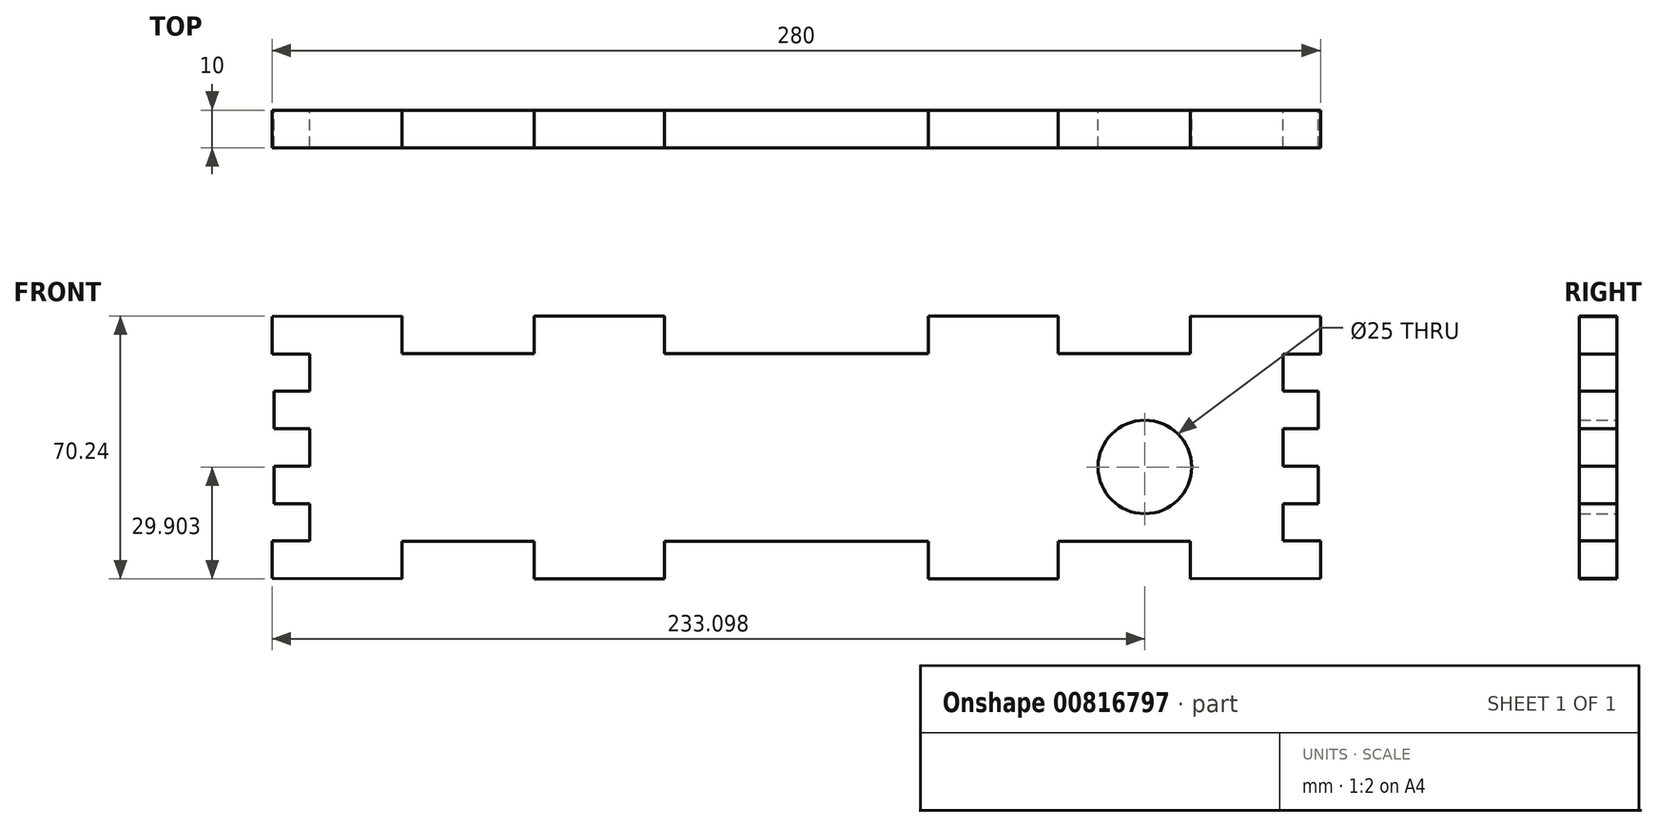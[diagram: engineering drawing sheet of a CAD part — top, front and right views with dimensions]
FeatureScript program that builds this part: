
annotation { "Feature Type Name" : "Feature", "Feature Type Description" : "" }
export const myFeature = defineFeature(function(context is Context, id is Id, definition is map)
    precondition{}
    {
        {
            var Q0;
            Q0=qCreatedBy(makeId("Front.planeOp"),FACE);
            var sketch = newSketch(context, id + "F0", { "sketchPlane" : qUnion([Q0])});
            skPoint(sketch, "E0.MirrorP", {"position": v(122.5, 95) * mm});
            skPoint(sketch, "E1.MirrorP", {"position": v(122.5, -95) * mm});
            skLineSegment(sketch, "E2", {"start": v(140, -35) * mm, "end": v(140, -25) * mm});
            skLineSegment(sketch, "E3", {"start": v(140, -25) * mm, "end": v(130, -25) * mm});
            skLineSegment(sketch, "E4", {"start": v(130, -25) * mm, "end": v(130, -15) * mm});
            skLineSegment(sketch, "E5", {"start": v(130, -15) * mm, "end": v(139.43, -15) * mm});
            skLineSegment(sketch, "E6", {"start": v(139.43, -15) * mm, "end": v(139.43, -5) * mm});
            skLineSegment(sketch, "E7", {"start": v(139.43, -5) * mm, "end": v(130, -5) * mm});
            skLineSegment(sketch, "E8.MirrorCS", {"start": v(139.43, 5) * mm, "end": v(130, 5) * mm});
            skLineSegment(sketch, "E9.MirrorCS", {"start": v(139.43, 15) * mm, "end": v(139.43, 5) * mm});
            skLineSegment(sketch, "E10.MirrorCS", {"start": v(130, 15) * mm, "end": v(139.43, 15) * mm});
            skLineSegment(sketch, "E11.MirrorCS", {"start": v(130, 25) * mm, "end": v(130, 15) * mm});
            skLineSegment(sketch, "E12.MirrorCS", {"start": v(140, 25) * mm, "end": v(130, 25) * mm});
            skLineSegment(sketch, "E13.MirrorCS", {"start": v(140, 35) * mm, "end": v(140, 25) * mm});
            skLineSegment(sketch, "E14.MirrorCS", {"start": v(-140, 35) * mm, "end": v(-140, 25) * mm});
            skLineSegment(sketch, "E15.MirrorCS", {"start": v(-140, -35) * mm, "end": v(-140, -25) * mm});
            skLineSegment(sketch, "E16.MirrorCS", {"start": v(-139.43, 15) * mm, "end": v(-139.43, 5) * mm});
            skLineSegment(sketch, "E17.MirrorCS", {"start": v(-139.43, -5) * mm, "end": v(-130, -5) * mm});
            skLineSegment(sketch, "E18.MirrorCS", {"start": v(-140, -25) * mm, "end": v(-130, -25) * mm});
            skLineSegment(sketch, "E19.MirrorCS", {"start": v(-130, -15) * mm, "end": v(-139.43, -15) * mm});
            skLineSegment(sketch, "E20.MirrorCS", {"start": v(-130, 15) * mm, "end": v(-139.43, 15) * mm});
            skLineSegment(sketch, "E21.MirrorCS", {"start": v(-140, 25) * mm, "end": v(-130, 25) * mm});
            skLineSegment(sketch, "E22.MirrorCS", {"start": v(-130, -25) * mm, "end": v(-130, -15) * mm});
            skLineSegment(sketch, "E23.MirrorCS", {"start": v(-139.43, -15) * mm, "end": v(-139.43, -5) * mm});
            skLineSegment(sketch, "E24.MirrorCS", {"start": v(-130, 25) * mm, "end": v(-130, 15) * mm});
            skLineSegment(sketch, "E25.MirrorCS", {"start": v(-139.43, 5) * mm, "end": v(-130, 5) * mm});
            skLineSegment(sketch, "E26", {"start": v(-130, 5) * mm, "end": v(-130, -5) * mm});
            skLineSegment(sketch, "E27", {"start": v(130, 5) * mm, "end": v(130, -5) * mm});
            skLineSegment(sketch, "E28", {"start": v(-140, -35) * mm, "end": v(-105.25, -35.12) * mm});
            skLineSegment(sketch, "E29", {"start": v(-105.25, -35.12) * mm, "end": v(-105.25, -25.12) * mm});
            skLineSegment(sketch, "E30", {"start": v(-105.25, -25.12) * mm, "end": v(-70, -25.12) * mm});
            skLineSegment(sketch, "E31", {"start": v(-70, -25.12) * mm, "end": v(-70, -35.12) * mm});
            skLineSegment(sketch, "E32", {"start": v(-70, -35.12) * mm, "end": v(-35.25, -35.12) * mm});
            skLineSegment(sketch, "E33", {"start": v(-35.25, -35.12) * mm, "end": v(-35.25, -25.12) * mm});
            skLineSegment(sketch, "E34", {"start": v(-35.25, -25.12) * mm, "end": v(0, -25.12) * mm});
            skLineSegment(sketch, "E35.MirrorCS", {"start": v(140, -35) * mm, "end": v(105.25, -35.12) * mm});
            skLineSegment(sketch, "E36.MirrorCS", {"start": v(105.25, -35.12) * mm, "end": v(105.25, -25.12) * mm});
            skLineSegment(sketch, "E37.MirrorCS", {"start": v(105.25, -25.12) * mm, "end": v(70, -25.12) * mm});
            skLineSegment(sketch, "E38.MirrorCS", {"start": v(70, -25.12) * mm, "end": v(70, -35.12) * mm});
            skLineSegment(sketch, "E39.MirrorCS", {"start": v(70, -35.12) * mm, "end": v(35.25, -35.12) * mm});
            skLineSegment(sketch, "E40.MirrorCS", {"start": v(35.25, -35.12) * mm, "end": v(35.25, -25.12) * mm});
            skLineSegment(sketch, "E41.MirrorCS", {"start": v(35.25, -25.12) * mm, "end": v(0, -25.12) * mm});
            skLineSegment(sketch, "E42.MirrorCS", {"start": v(-140, 35) * mm, "end": v(-105.25, 35.12) * mm});
            skLineSegment(sketch, "E43.MirrorCS", {"start": v(-105.25, 25.12) * mm, "end": v(-70, 25.12) * mm});
            skLineSegment(sketch, "E44.MirrorCS", {"start": v(-70, 25.12) * mm, "end": v(-70, 35.12) * mm});
            skLineSegment(sketch, "E45.MirrorCS", {"start": v(-105.25, 35.12) * mm, "end": v(-105.25, 25.12) * mm});
            skLineSegment(sketch, "E46.MirrorCS", {"start": v(-70, 35.12) * mm, "end": v(-35.25, 35.12) * mm});
            skLineSegment(sketch, "E47.MirrorCS", {"start": v(-35.25, 35.12) * mm, "end": v(-35.25, 25.12) * mm});
            skLineSegment(sketch, "E48.MirrorCS", {"start": v(-35.25, 25.12) * mm, "end": v(0, 25.12) * mm});
            skLineSegment(sketch, "E49.MirrorCS", {"start": v(35.25, 25.12) * mm, "end": v(0, 25.12) * mm});
            skLineSegment(sketch, "E50.MirrorCS", {"start": v(35.25, 35.12) * mm, "end": v(35.25, 25.12) * mm});
            skLineSegment(sketch, "E51.MirrorCS", {"start": v(70, 35.12) * mm, "end": v(35.25, 35.12) * mm});
            skLineSegment(sketch, "E52.MirrorCS", {"start": v(70, 25.12) * mm, "end": v(70, 35.12) * mm});
            skLineSegment(sketch, "E53.MirrorCS", {"start": v(105.25, 25.12) * mm, "end": v(70, 25.12) * mm});
            skLineSegment(sketch, "E54.MirrorCS", {"start": v(105.25, 35.12) * mm, "end": v(105.25, 25.12) * mm});
            skLineSegment(sketch, "E55.MirrorCS", {"start": v(140, 35) * mm, "end": v(105.25, 35.12) * mm});
            skCircle(sketch, "E56", {"center": v(93.1, -5.22) * mm, "radius": 12.5 * mm});
            skSolve(sketch);
        }
        {
            var Q0;
            Q0=makeQuery(id+"F0.imprint","IMPRINT",FACE,{"disambiguationData":[TD([[makeQuery(id+"F0.imprint","IMPRINT",EDGE,{"derivedFrom":sQuery(id+"F0.wireOp",EDGE,"E2")}),1.0]])]});
            extrude(context, id + "F1", {"entities" : qUnion([Q0]), "depth" : 10 * mm, "offsetDistance" : 25 * mm});
        }
    });
